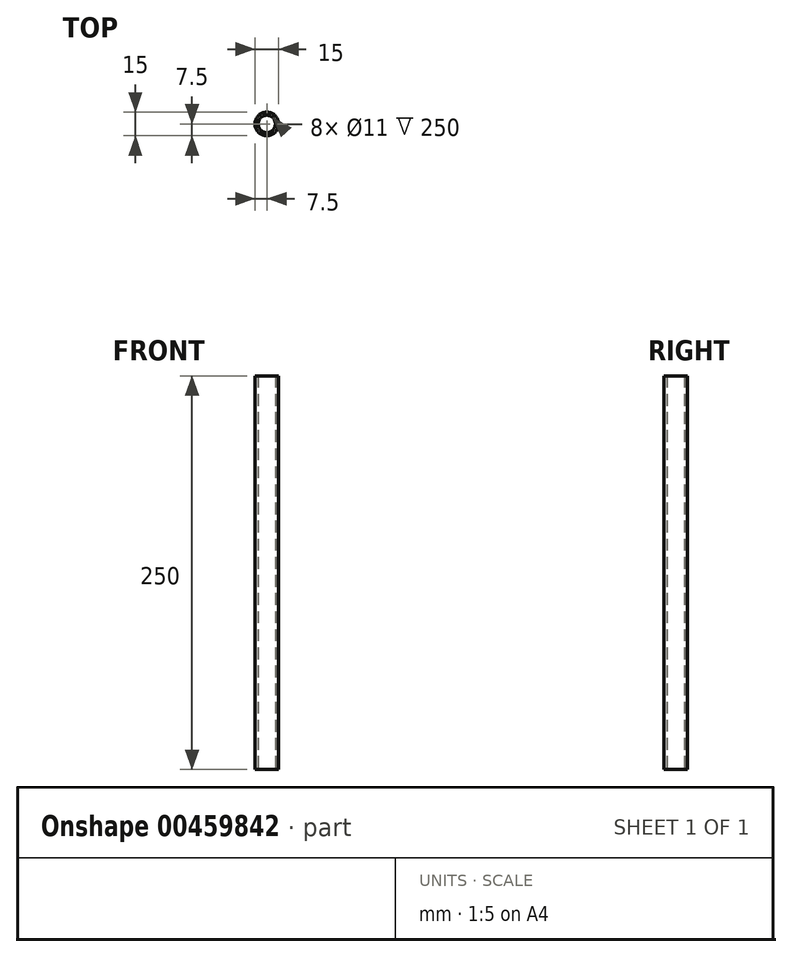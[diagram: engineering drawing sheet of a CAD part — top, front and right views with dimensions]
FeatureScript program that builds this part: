
annotation { "Feature Type Name" : "Feature", "Feature Type Description" : "" }
export const myFeature = defineFeature(function(context is Context, id is Id, definition is map)
    precondition{}
    {
        {
            var Q0;
            Q0=qCreatedBy(makeId("Top.planeOp"),FACE);
            var sketch = newSketch(context, id + "F0", { "sketchPlane" : qUnion([Q0])});
            skCircle(sketch, "E0", {"center": v(0, 0) * mm, "radius": 5.5 * mm});
            skCircle(sketch, "E1", {"center": v(0, 0) * mm, "radius": 7.5 * mm});
            skSolve(sketch);
        }
        {
            var Q0;
            Q0 = qSketchRegion(id + "F0", true);
            extrude(context, id + "F1", {"entities" : qUnion([Q0]), "depth" : 250 * mm, "offsetDistance" : 25 * mm});
        }
    });
